# Revit family: Sanitary_Bath&Spas_Kaldewei_Saniform-Plus_750x1600x410
name_source: partatom
category: Plumbing Fixtures
revit_build: Autodesk Revit 2015 (Build: 20140606_1530(x64)
units: mm (PartAtom-declared; Revit-internal decimal feet)

## types (1)
- Sanitary_Bath&Spas_Kaldewei_Saniform-Plus_750x1600x410
    Accessoire = Yes
    BIMobject category = Bath & Spas
    Brand url = http://www.kaldewei.com
    Chrome = Chrome
    Color = https://www.kaldewei.co.uk
    ColourOptions = https://www.kaldewei.co.uk
    ConnectingDimensions = EN 232
    Design country = Germany
    DrainSize = 52 mm
    Durability = https://www.kaldewei.de
    Edition number = 1
    Features = https://www.kaldewei.co.uk
    Finish = https://www.kaldewei.co.uk
    Finition = Kaldewei
    HasGrabHandles = https://www.kaldewei.co.uk
    IFC Classification = Furnishing Element
    IfcExportAs = BATH
    IfcExportType = IfcSanitaryTerminalType
    IntegralAccessories = https://www.kaldewei.co.uk
    Manufacturer = Kaldewei
    Manufacturer country = Germany
    ManufacturerCountry = GERMANY
    ManufacturerName = KALDEWEI
    ManufacturerURL = https://www.kaldewei.com
    Material = steel enamel
    Material main = Steel
    Material secondary = Enamel
    Model = SANIFORM PLUS
    NBS Reference Code = 35-06-08
    NBS Reference Description = Baths
    Name = SANIFORM PLUS
    Nominal height = 750 cm
    Nominal width = 1600 cm
    NominalDepth = 410
    NominalLength = 1600
    ObjectName = SANIFORM PLUS 750x1600x410
    ObjectNorm = EN 14516EU DECLARATION OF PERFORMANCE(https://www.kaldewei.de
    ObjectPicture = https://www.kaldewei.co.uk
    ObjectURL = https://www.kaldewei.co.uk
    Polantis code = KDW010029
    Product Guid = 379613ea-a453-4719-9286-305f0deac98d
    Product SKU = 372
    Product certification = https://www.kaldewei.co.uk
    Product data url = http://bimobject.com
    Product family = SANIFORM
    Product group = Bathtub
    Product url = https://www.kaldewei.co.uk
    ProductInformation = Model No.372: There are shapes that have simply become a part of our everyday lives. Like the one-person SANIFORM baths with the waste positioned at the foot end, one of the classic baths designed to fit the human body, which look good in any bathroom. Regardless of which model you choose, the especially broad back area and the ergonomic form mean you can always bathe in perfect comfort.
    QR code = http://bimobject.com
    Revision = 1
    SerialNumber = 372
    Shape = Rectangular baths
    Size = 750x1600x410
    SupportFrame = https://www.kaldewei.co.uk
    Sustainability = https://kaldewei-fa.secure.footprint.net
    Technical description = https://www.kaldewei.co.uk
    TechnicalDataURL = https://kaldewei.typo-live.web-factory.de
    Type Comments = SANIFORM PLUS 372-1 750x1600x410
    UNSPSC Code = 30181501
    UNSPSCCode = 30181500
    UNSPSCNames = Sanitary ware
    URL = https://www.kaldewei.co.uk
    Uniclass 1.4 Code = L7211
    Uniclass 1.4 Description = Baths
    Uniclass 2.0 Code = PR-35-06-08
    Uniclass 2.0 Description = Baths
    Uniclass 2015 = Pr_40_20_06_08
    Version = 5
    VolumeToOverflowMaximum = 107
    WarrantyDurationParts = 30
    WarrantyDurationUnit = Year
    WarrantyStartDate = https://www.kaldewei.co.uk
    WaterSupplyOverflowAndWasteHolesOverflow = 52 mm
    WaterSupplyOverflowAndWasteHolesWaste = 52 mm
    Weight = 47
    Weight Net (Kg) = 47

## geometry (parser evidence)
native form markers: Sweep x11
no freeform markers — native parametric forms only
